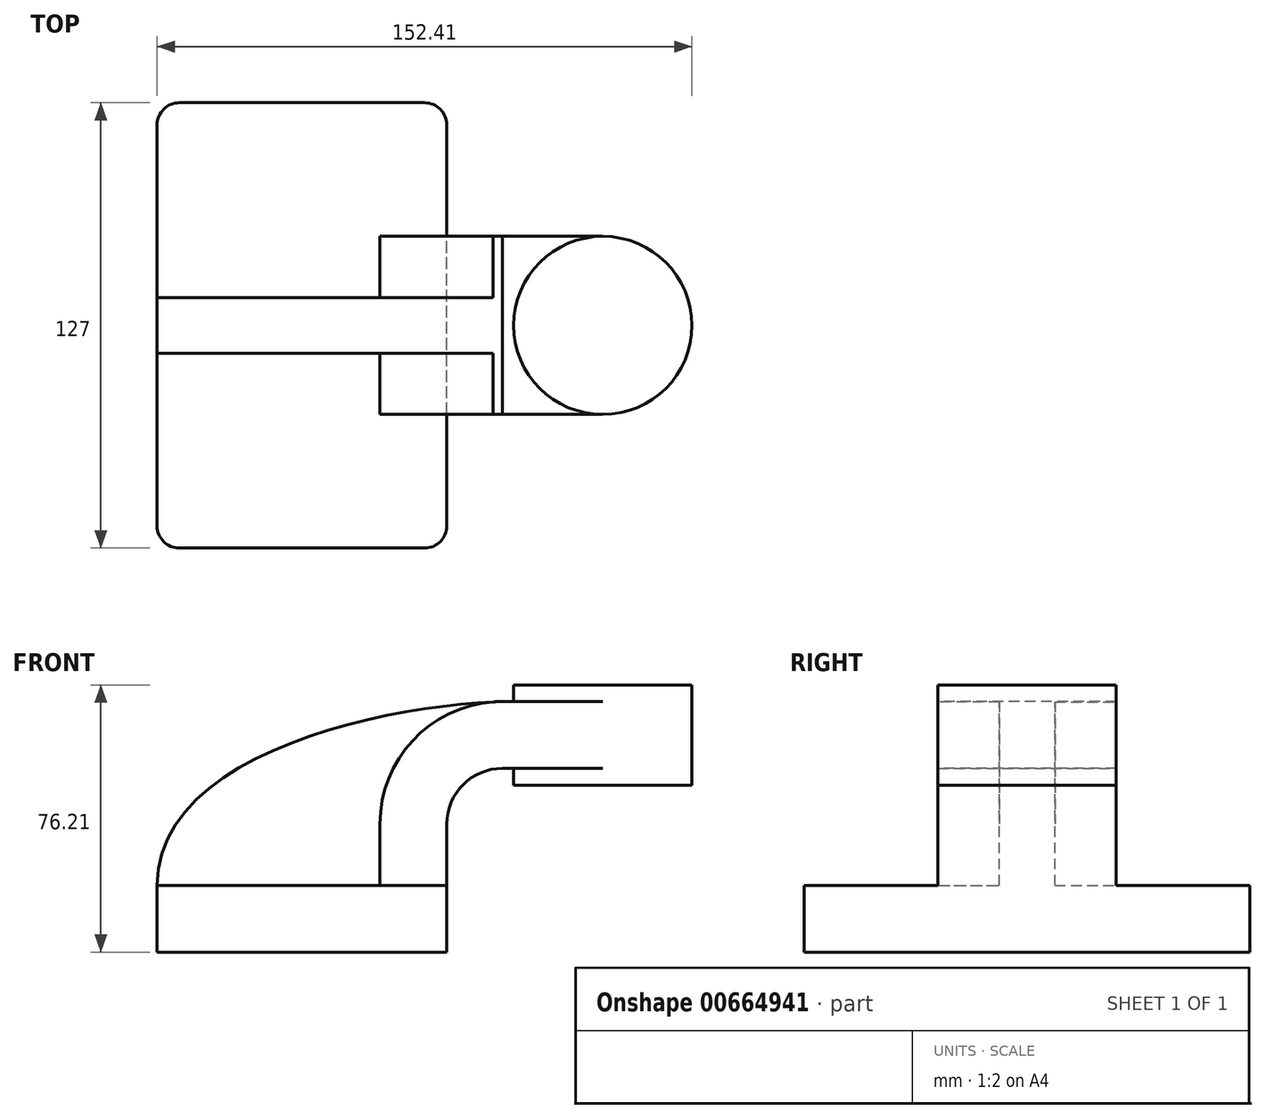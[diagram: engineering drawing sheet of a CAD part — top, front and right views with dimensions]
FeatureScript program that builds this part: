
annotation { "Feature Type Name" : "Feature", "Feature Type Description" : "" }
export const myFeature = defineFeature(function(context is Context, id is Id, definition is map)
    precondition{}
    {
        {
            var Q0;
            Q0=qCreatedBy(makeId("Front.planeOp"),FACE);
            var sketch = newSketch(context, id + "F0", { "sketchPlane" : qUnion([Q0])});
            skLineSegment(sketch, "E0.bottom", {"start": v(-41.28, 9.52) * mm, "end": v(41.28, 9.53) * mm});
            skLineSegment(sketch, "E0.top", {"start": v(-41.28, -9.53) * mm, "end": v(41.28, -9.53) * mm});
            skLineSegment(sketch, "E0.left", {"start": v(-41.28, 9.52) * mm, "end": v(-41.28, -9.53) * mm});
            skLineSegment(sketch, "E0.right", {"start": v(41.28, 9.53) * mm, "end": v(41.28, -9.52) * mm});
            skPoint(sketch, "E0.middle", {"position": v(0, 0) * mm});
            skLineSegment(sketch, "E1.bottom", {"start": v(60.32, 66.67) * mm, "end": v(111.12, 66.67) * mm});
            skLineSegment(sketch, "E1.top", {"start": v(60.32, 38.1) * mm, "end": v(111.13, 38.1) * mm});
            skLineSegment(sketch, "E1.left", {"start": v(60.32, 66.67) * mm, "end": v(60.32, 38.1) * mm});
            skLineSegment(sketch, "E1.right", {"start": v(111.12, 66.67) * mm, "end": v(111.12, 38.1) * mm});
            skPoint(sketch, "E1.middle", {"position": v(85.72, 52.39) * mm});
            skLineSegment(sketch, "E2", {"start": v(41.27, 9.53) * mm, "end": v(41.27, 27) * mm});
            skArc(sketch, "E3", {"start": v(41.27, 27) * mm, "mid": v(45.92, 38.23) * mm, "end": v(57.15, 42.88) * mm});
            skLineSegment(sketch, "E4", {"start": v(57.15, 42.88) * mm, "end": v(85.73, 42.88) * mm});
            skPoint(sketch, "E4.endSnap0", {"position": v(85.73, 38.1) * mm});
            skLineSegment(sketch, "E5.0", {"start": v(57.15, 61.93) * mm, "end": v(85.72, 61.93) * mm});
            skArc(sketch, "E5.1", {"start": v(22.22, 27) * mm, "mid": v(32.45, 51.7) * mm, "end": v(57.15, 61.93) * mm});
            skLineSegment(sketch, "E5.2", {"start": v(22.22, 9.53) * mm, "end": v(22.22, 27) * mm});
            skFitSpline(sketch, "E6", {"points": [v(-41.28, 9.52) * mm, v(57.15, 61.93) * mm], "startDerivative": vector(0.09, 114.1) * mm, "endDerivative": vector(97.28, 2.8) * mm});
            skLineSegment(sketch, "E7", {"start": v(85.73, 66.68) * mm, "end": v(85.73, 38.1) * mm});
            skSolve(sketch);
        }
        {
            var Q0;
            Q0=makeQuery(id+"F0.imprint","IMPRINT",FACE,{"disambiguationData":[TD([[makeQuery(id+"F0.imprint","IMPRINT",EDGE,{"derivedFrom":sQuery(id+"F0.wireOp",EDGE,"E0.top")}),1.0]])]});
            extrude(context, id + "F1", {"entities" : qUnion([Q0]), "endBound" : BoundingType.SYMMETRIC, "depth" : 127 * mm, "offsetDistance" : 25.4 * mm});
        }
        {
            var Q0;
            {var subQ1=sQuery(id+"F0.wireOp",EDGE,"E2");Q0=makeQuery(id+"F0.imprint","IMPRINT",FACE,{"disambiguationData":[TD([[makeQuery(id+"F0.imprint","IMPRINT",EDGE,{"derivedFrom":subQ1}),1.0]])]});}
            var Q1;
            {var subQ0=sQuery(id+"F0.wireOp",EDGE,"E5.0");var subQ1=sQuery(id+"F0.wireOp",EDGE,"E1.left");var subQ2=makeQuery(id+"F0.imprint","INTERSECT",VERTEX,{"derivedFrom":[subQ1,subQ0]});Q1=makeQuery(id+"F0.imprint","IMPRINT",FACE,{"disambiguationData":[TD([[makeQuery(id+"F0.imprint","IMPRINT",EDGE,{"disambiguationData":[TD([[subQ2,-1.0]])],"derivedFrom":subQ1}),1.0]])]});}
            extrude(context, id + "F2", {"entities" : qUnion([Q0, Q1]), "operationType" : NewBodyOperationType.ADD, "endBound" : BoundingType.SYMMETRIC, "depth" : 50.8 * mm, "offsetDistance" : 25.4 * mm});
        }
        {
            var Q0;
            {var subQ3=sQuery(id+"F0.wireOp",EDGE,"E5.2");Q0=makeQuery(id+"F0.imprint","IMPRINT",FACE,{"disambiguationData":[TD([[makeQuery(id+"F0.imprint","IMPRINT",EDGE,{"derivedFrom":subQ3}),1.0]])]});}
            extrude(context, id + "F3", {"entities" : qUnion([Q0]), "operationType" : NewBodyOperationType.ADD, "endBound" : BoundingType.SYMMETRIC, "depth" : 15.88 * mm, "offsetDistance" : 25.4 * mm});
        }
        {
            var Q0;
            Q0=makeQuery(id+"F1.opExtrude","CAP_EDGE",EDGE,{"disambiguationData":[OSD([sQuery(id+"F0.wireOp",EDGE,"E0.right")])],"isStart":false});
            var Q1;
            Q1=makeQuery(id+"F1.opExtrude","CAP_EDGE",EDGE,{"disambiguationData":[OSD([sQuery(id+"F0.wireOp",EDGE,"E0.left")])],"isStart":false});
            var Q2;
            Q2=makeQuery(id+"F1.opExtrude","CAP_EDGE",EDGE,{"disambiguationData":[OSD([sQuery(id+"F0.wireOp",EDGE,"E0.right")])],"isStart":true});
            var Q3;
            Q3=makeQuery(id+"F1.opExtrude","CAP_EDGE",EDGE,{"disambiguationData":[OSD([sQuery(id+"F0.wireOp",EDGE,"E0.left")])],"isStart":true});
            fillet(context, id + "F4", {"entities" : qUnion([Q0, Q1, Q2, Q3]), "radius" : 6.35 * mm, "tangentPropagation" : true, "allowEdgeOverflow" : false});
        }
        {
            var Q0;
            {var subQ4=sQuery(id+"F0.wireOp",EDGE,"E1.right");Q0=makeQuery(id+"F0.imprint","IMPRINT",FACE,{"disambiguationData":[TD([[makeQuery(id+"F0.imprint","IMPRINT",EDGE,{"derivedFrom":subQ4}),-1.0]])]});}
            var Q1;
            Q1=sQuery(id+"F0.wireOp",EDGE,"E7");
            revolve(context, id + "F5", {"operationType" : NewBodyOperationType.ADD, "entities" : qUnion([Q0]), "axis" : qUnion([Q1]), "revolveType" : RevolveType.FULL});
        }
    });
